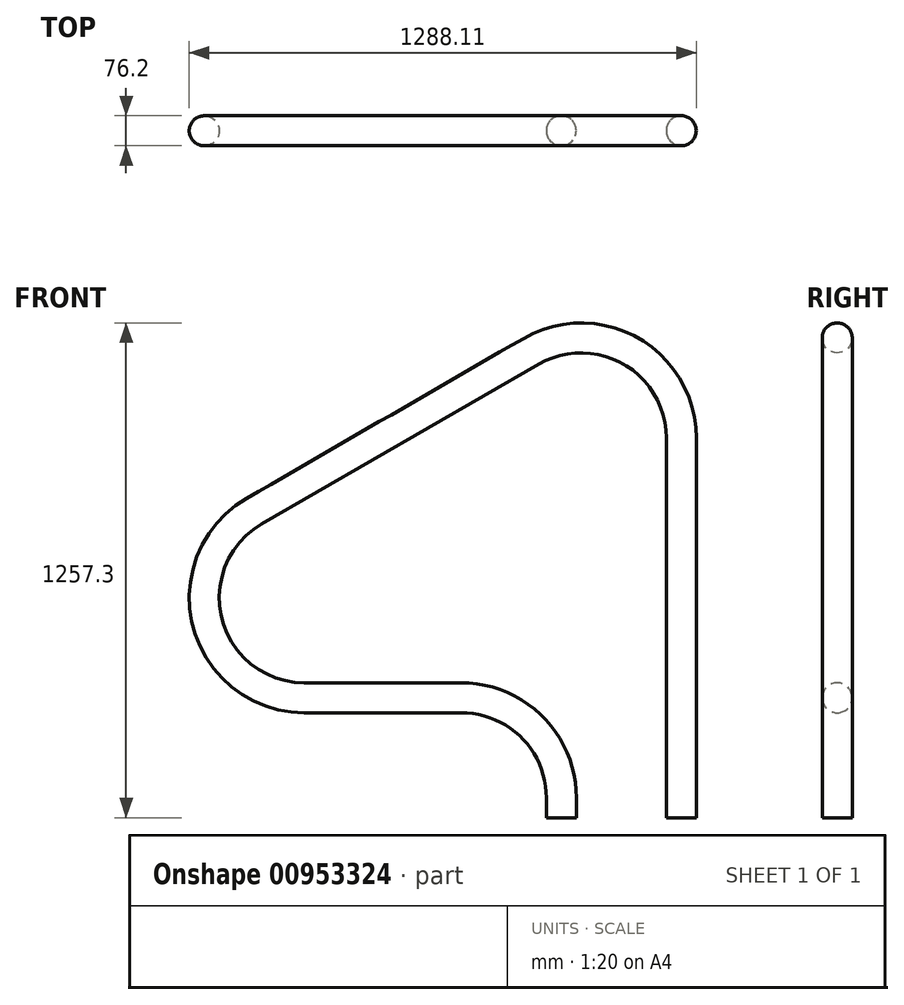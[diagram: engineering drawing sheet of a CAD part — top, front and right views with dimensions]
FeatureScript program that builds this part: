
annotation { "Feature Type Name" : "Feature", "Feature Type Description" : "" }
export const myFeature = defineFeature(function(context is Context, id is Id, definition is map)
    precondition{}
    {
        {
            var Q0;
            Q0=qCreatedBy(makeId("Front.planeOp"),FACE);
            var sketch = newSketch(context, id + "F0", { "sketchPlane" : qUnion([Q0])});
            skLineSegment(sketch, "E0", {"start": v(0, 0) * mm, "end": v(0, 965.2) * mm});
            skLineSegment(sketch, "E1", {"start": v(-381, 1185.17) * mm, "end": v(-1084.9, 778.77) * mm});
            skLineSegment(sketch, "E2", {"start": v(-957.9, 304.8) * mm, "end": v(-558.8, 304.8) * mm});
            skLineSegment(sketch, "E3", {"start": v(-304.8, 50.8) * mm, "end": v(-304.8, 0) * mm});
            skPoint(sketch, "E4.visualSharp", {"position": v(0, 1405.14) * mm});
            skArc(sketch, "E4.filletArc", {"start": v(0, 965.2) * mm, "mid": v(-127, 1185.17) * mm, "end": v(-381, 1185.17) * mm});
            skPoint(sketch, "E5.visualSharp", {"position": v(-1905.85, 304.8) * mm});
            skArc(sketch, "E5.filletArc", {"start": v(-1084.9, 778.77) * mm, "mid": v(-1203.25, 493.06) * mm, "end": v(-957.9, 304.8) * mm});
            skPoint(sketch, "E6.visualSharp", {"position": v(-304.8, 304.8) * mm});
            skArc(sketch, "E6.filletArc", {"start": v(-304.8, 50.8) * mm, "mid": v(-379.2, 230.4) * mm, "end": v(-558.8, 304.8) * mm});
            skLineSegment(sketch, "E7", {"start": v(-522.98, 1219.2) * mm, "end": v(44.84, 1219.2) * mm, "construction": true});
            skSolve(sketch);
        }
        {
            var Q0;
            Q0=sQuery(id+"F0.wireOp",VERTEX,"E0.start");
            var Q1;
            Q1=sQuery(id+"F0.wireOp",EDGE,"E0");
            cPlane(context, id + "F1", {"entities" : qUnion([Q0, Q1]), "cplaneType" : CPlaneType.LINE_POINT, "offset" : 25.4 * mm, "width" : 152.4 * mm, "height" : 152.4 * mm});
        }
        {
            var Q0;
            Q0=qCreatedBy(id+"F1.planeOp",FACE);
            var sketch = newSketch(context, id + "F2", { "sketchPlane" : qUnion([Q0])});
            skCircle(sketch, "E8", {"center": v(0, 0) * mm, "radius": 38.1 * mm});
            skSolve(sketch);
        }
        {
            var Q0;
            Q0=makeQuery(id+"F2.imprint","IMPRINT",FACE,{"disambiguationData":[TD([[makeQuery(id+"F2.imprint","IMPRINT",EDGE,{"derivedFrom":sQuery(id+"F2.wireOp",EDGE,"E8")}),1.0]])]});
            var Q1;
            Q1 = qConstructionFilter(qBodyType(qCreatedBy(id + "F0" ,EDGE), BodyType.WIRE), ConstructionObject.NO);
            sweep(context, id + "F3", {"profiles" : qUnion([Q0]), "path" : qUnion([Q1])});
        }
    });
